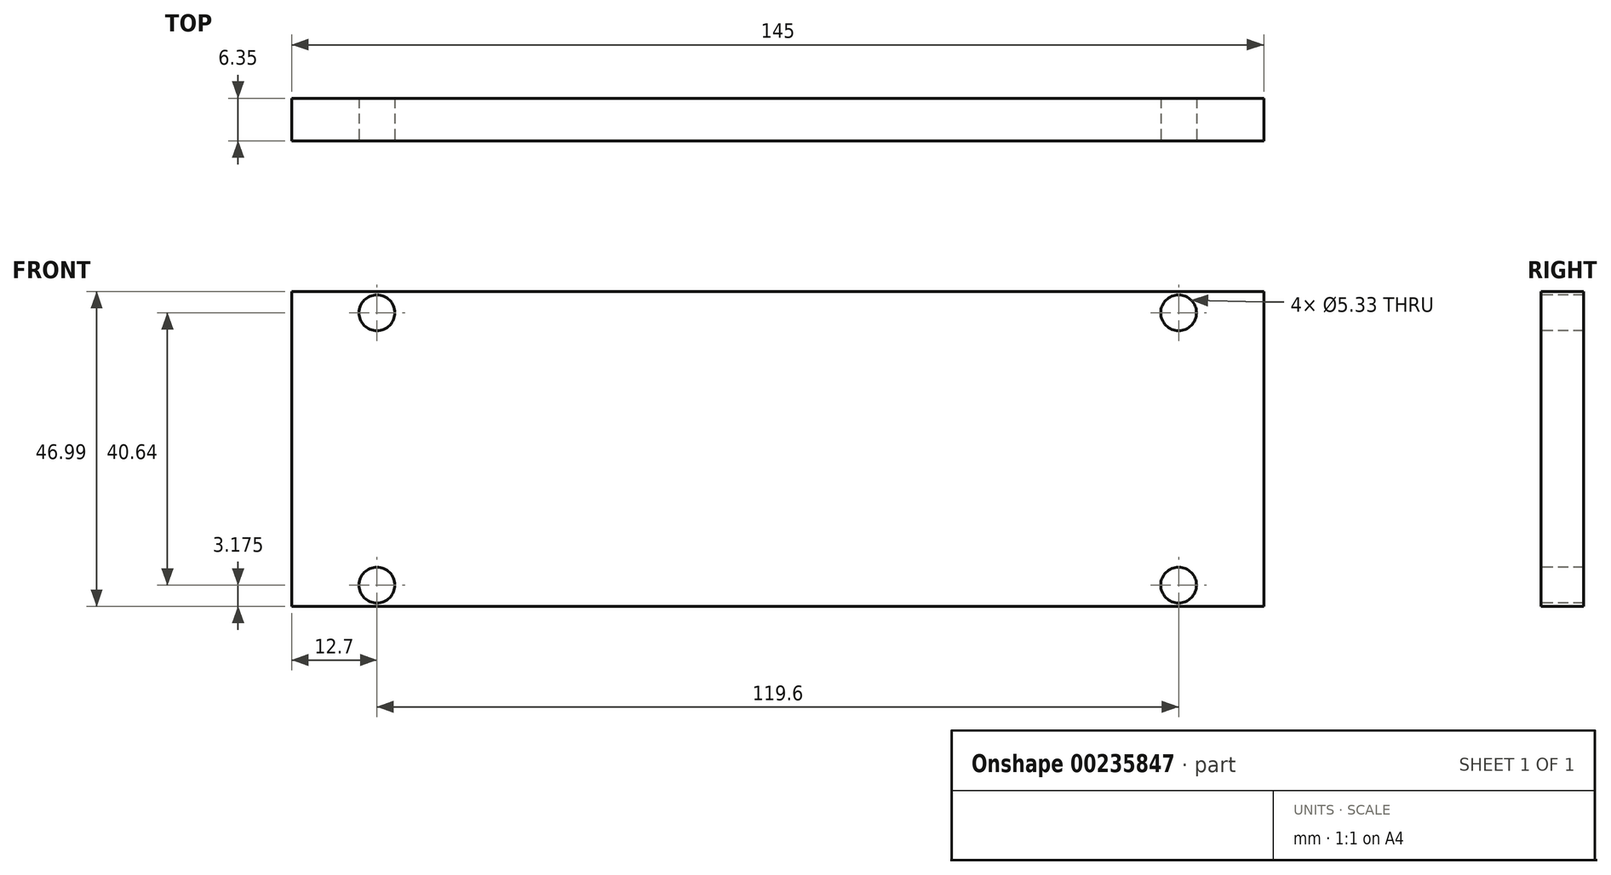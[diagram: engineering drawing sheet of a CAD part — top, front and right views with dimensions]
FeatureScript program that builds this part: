
annotation { "Feature Type Name" : "Feature", "Feature Type Description" : "" }
export const myFeature = defineFeature(function(context is Context, id is Id, definition is map)
    precondition{}
    {
        {
            var Q0;
            Q0=qCreatedBy(makeId("Front.planeOp"),FACE);
            var sketch = newSketch(context, id + "F0", { "sketchPlane" : qUnion([Q0])});
            skLineSegment(sketch, "E0.bottom", {"start": v(0, 0) * mm, "end": v(145, 0) * mm});
            skLineSegment(sketch, "E0.top", {"start": v(0, 47) * mm, "end": v(145, 47) * mm});
            skLineSegment(sketch, "E0.left", {"start": v(0, 0) * mm, "end": v(0, 47) * mm});
            skLineSegment(sketch, "E0.right", {"start": v(145, 0) * mm, "end": v(145, 47) * mm});
            skSolve(sketch);
        }
        {
            var Q0;
            Q0=makeQuery(id+"F0.imprint","IMPRINT",FACE,{"disambiguationData":[TD([[makeQuery(id+"F0.imprint","IMPRINT",EDGE,{"derivedFrom":sQuery(id+"F0.wireOp",EDGE,"E0.bottom")}),1.0]])]});
            extrude(context, id + "F1", {"entities" : qUnion([Q0]), "depth" : 6.35 * mm});
        }
        {
            var Q0;
            Q0=makeQuery(id+"F1.opExtrude","CAP_FACE",FACE,{"disambiguationData":[OSD([sQuery(id+"F0.wireOp",EDGE,"E0.bottom"),sQuery(id+"F0.wireOp",EDGE,"E0.top"),sQuery(id+"F0.wireOp",EDGE,"E0.left"),sQuery(id+"F0.wireOp",EDGE,"E0.right")])],"isStart":false});
            var sketch = newSketch(context, id + "F2", { "sketchPlane" : qUnion([Q0])});
            skPoint(sketch, "E1", {"position": v(12.7, 43.82) * mm});
            skPoint(sketch, "E2", {"position": v(132.3, 43.82) * mm});
            skPoint(sketch, "E3", {"position": v(12.7, 3.18) * mm});
            skPoint(sketch, "E4", {"position": v(132.3, 3.18) * mm});
            skSolve(sketch);
        }
        {
            var Q0;
            Q0=sQuery(id+"F2.wireOp",VERTEX,"E1");
            var Q1;
            Q1=sQuery(id+"F2.wireOp",VERTEX,"E2");
            var Q2;
            Q2=sQuery(id+"F2.wireOp",VERTEX,"E3");
            var Q3;
            Q3=sQuery(id+"F2.wireOp",VERTEX,"E4");
            var Q4;
            Q4=makeQuery(id+"F1.opExtrude","SWEPT_BODY",BODY,{"disambiguationData":[OSD([sQuery(id+"F0.wireOp",EDGE,"E0.bottom"),sQuery(id+"F0.wireOp",EDGE,"E0.top"),sQuery(id+"F0.wireOp",EDGE,"E0.left"),sQuery(id+"F0.wireOp",EDGE,"E0.right")])]});
            hole(context, id + "F3", {"style" : HoleStyle.SIMPLE, "endStyle" : HoleEndStyle.BLIND, "holeDiameter" : 5.33 * mm, "holeDepth" : 76.2 * mm, "locations" : qUnion([Q0, Q1, Q2, Q3]), "scope" : qUnion([Q4])});
        }
    });
